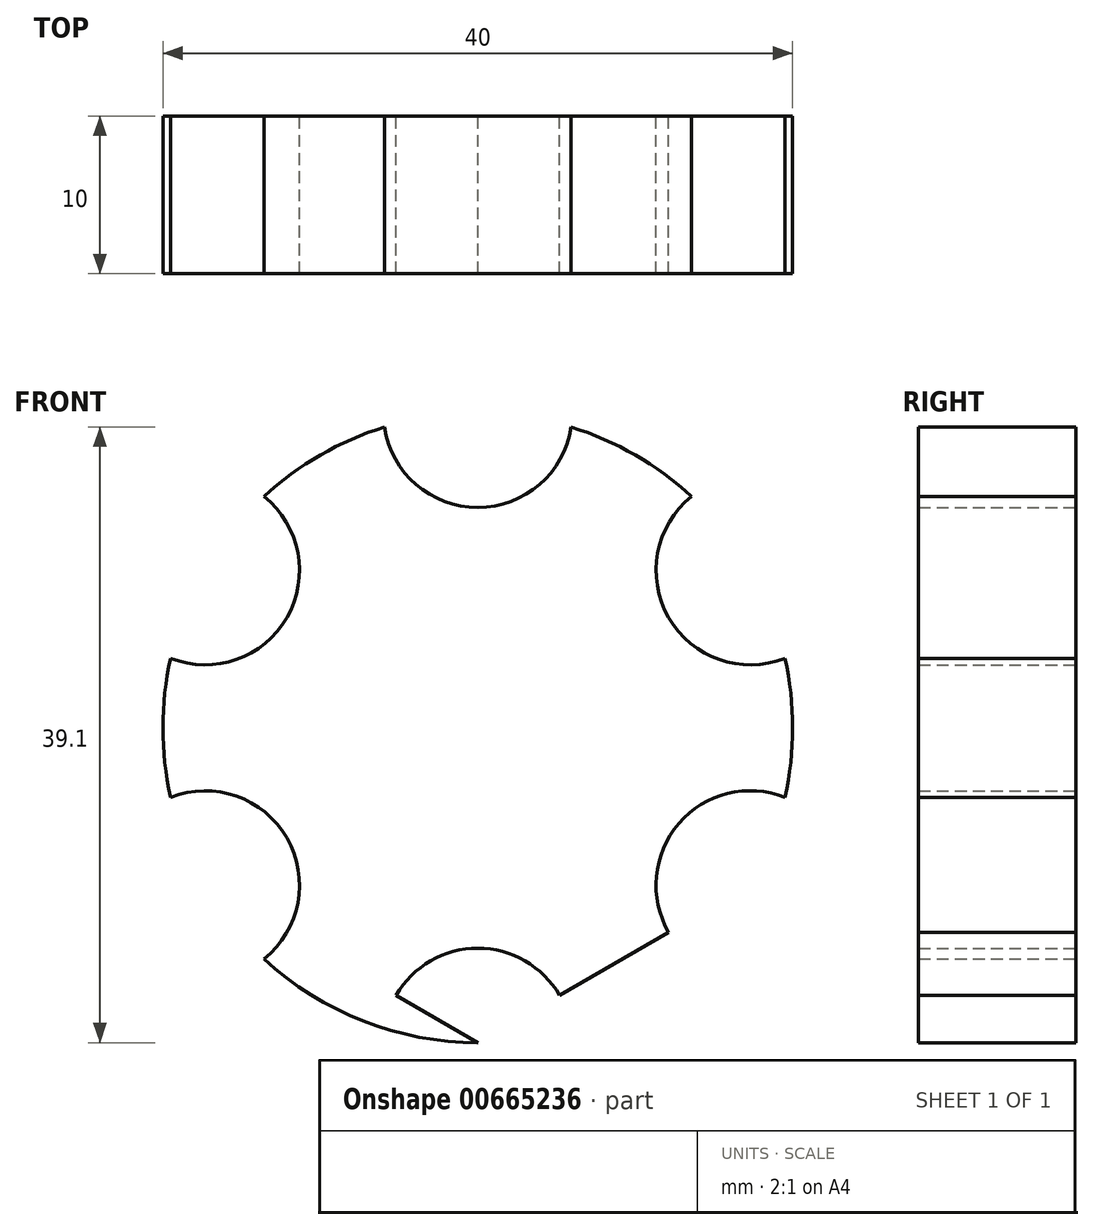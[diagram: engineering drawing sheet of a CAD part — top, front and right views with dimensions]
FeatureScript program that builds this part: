
annotation { "Feature Type Name" : "Feature", "Feature Type Description" : "" }
export const myFeature = defineFeature(function(context is Context, id is Id, definition is map)
    precondition{}
    {
        {
            var Q0;
            Q0=qCreatedBy(makeId("Front.planeOp"),FACE);
            cPlane(context, id + "F0", {"entities" : qUnion([Q0]), "cplaneType" : CPlaneType.OFFSET, "offset" : 20 * mm, "oppositeDirection" : true, "width" : 150 * mm, "height" : 150 * mm});
        }
        {
            var Q0;
            Q0=qCreatedBy(id+"F0.planeOp",FACE);
            var sketch = newSketch(context, id + "F1", { "sketchPlane" : qUnion([Q0])});
            skCircle(sketch, "E0", {"center": v(0, 0) * mm, "radius": 20 * mm});
            skCircle(sketch, "E1.cCircle", {"center": v(0, 0) * mm, "radius": 20 * mm, "construction": true});
            skLineSegment(sketch, "E1.0", {"start": v(0, 20) * mm, "end": v(17.32, 10) * mm});
            skLineSegment(sketch, "E1.1", {"start": v(17.32, 10) * mm, "end": v(17.32, -10) * mm});
            skLineSegment(sketch, "E1.2", {"start": v(17.32, -10) * mm, "end": v(0, -20) * mm});
            skLineSegment(sketch, "E1.3", {"start": v(0, -20) * mm, "end": v(-17.32, -10) * mm});
            skLineSegment(sketch, "E1.4", {"start": v(-17.32, -10) * mm, "end": v(-17.32, 10) * mm});
            skLineSegment(sketch, "E1.5", {"start": v(-17.32, 10) * mm, "end": v(0, 20) * mm});
            skCircle(sketch, "E2", {"center": v(0, 20) * mm, "radius": 6 * mm});
            skCircle(sketch, "E3", {"center": v(17.32, 10) * mm, "radius": 6 * mm});
            skCircle(sketch, "E4", {"center": v(0, -20) * mm, "radius": 6 * mm});
            skCircle(sketch, "E5", {"center": v(-17.32, 10) * mm, "radius": 6 * mm});
            skCircle(sketch, "E6", {"center": v(-17.32, -10) * mm, "radius": 6 * mm});
            skCircle(sketch, "E7", {"center": v(17.32, -10) * mm, "radius": 6 * mm});
            skSolve(sketch);
        }
        {
            var Q0;
            {var subQ0=sQuery(id+"F1.wireOp",EDGE,"E3");var subQ1=sQuery(id+"F1.wireOp",EDGE,"E0");var subQ2=makeQuery(id+"F1.imprint","INTERSECT",VERTEX,{"disambiguationData":[OD(1.0)],"derivedFrom":[subQ1,subQ0]});Q0=makeQuery(id+"F1.imprint","IMPRINT",FACE,{"disambiguationData":[TD([[makeQuery(id+"F1.imprint","IMPRINT",EDGE,{"disambiguationData":[TD([[subQ2,-1.0]])],"derivedFrom":subQ1}),1.0]])]});}
            var Q1;
            {var subQ0=sQuery(id+"F1.wireOp",EDGE,"E3");var subQ1=sQuery(id+"F1.wireOp",EDGE,"E0");var subQ2=makeQuery(id+"F1.imprint","INTERSECT",VERTEX,{"disambiguationData":[OD(0.0)],"derivedFrom":[subQ1,subQ0]});Q1=makeQuery(id+"F1.imprint","IMPRINT",FACE,{"disambiguationData":[TD([[makeQuery(id+"F1.imprint","IMPRINT",EDGE,{"disambiguationData":[TD([[subQ2,1.0]])],"derivedFrom":subQ1}),1.0]])]});}
            var Q2;
            {var subQ10=sQuery(id+"F1.wireOp",EDGE,"E2");var subQ11=sQuery(id+"F1.wireOp",EDGE,"E1.0");var subQ12=makeQuery(id+"F1.imprint","INTERSECT",VERTEX,{"derivedFrom":[subQ11,subQ10]});Q2=makeQuery(id+"F1.imprint","IMPRINT",FACE,{"disambiguationData":[TD([[makeQuery(id+"F1.imprint","IMPRINT",EDGE,{"disambiguationData":[TD([[subQ12,-1.0]])],"derivedFrom":subQ11}),-1.0]])]});}
            var Q3;
            {var subQ0=sQuery(id+"F1.wireOp",EDGE,"E4");var subQ1=sQuery(id+"F1.wireOp",EDGE,"E0");var subQ2=makeQuery(id+"F1.imprint","INTERSECT",VERTEX,{"disambiguationData":[OD(1.0)],"derivedFrom":[subQ1,subQ0]});Q3=makeQuery(id+"F1.imprint","IMPRINT",FACE,{"disambiguationData":[TD([[makeQuery(id+"F1.imprint","IMPRINT",EDGE,{"disambiguationData":[TD([[subQ2,-1.0]])],"derivedFrom":subQ1}),1.0]])]});}
            var Q4;
            {var subQ0=sQuery(id+"F1.wireOp",EDGE,"E6");var subQ1=sQuery(id+"F1.wireOp",EDGE,"E0");var subQ2=makeQuery(id+"F1.imprint","INTERSECT",VERTEX,{"disambiguationData":[OD(1.0)],"derivedFrom":[subQ1,subQ0]});Q4=makeQuery(id+"F1.imprint","IMPRINT",FACE,{"disambiguationData":[TD([[makeQuery(id+"F1.imprint","IMPRINT",EDGE,{"disambiguationData":[TD([[subQ2,-1.0]])],"derivedFrom":subQ1}),1.0]])]});}
            var Q5;
            {var subQ0=sQuery(id+"F1.wireOp",EDGE,"E2");var subQ1=sQuery(id+"F1.wireOp",EDGE,"E0");var subQ2=makeQuery(id+"F1.imprint","INTERSECT",VERTEX,{"disambiguationData":[OD(1.0)],"derivedFrom":[subQ1,subQ0]});Q5=makeQuery(id+"F1.imprint","IMPRINT",FACE,{"disambiguationData":[TD([[makeQuery(id+"F1.imprint","IMPRINT",EDGE,{"disambiguationData":[TD([[subQ2,-1.0]])],"derivedFrom":subQ1}),1.0]])]});}
            var Q6;
            {var subQ0=sQuery(id+"F1.wireOp",EDGE,"E5");var subQ1=sQuery(id+"F1.wireOp",EDGE,"E0");var subQ2=makeQuery(id+"F1.imprint","INTERSECT",VERTEX,{"disambiguationData":[OD(1.0)],"derivedFrom":[subQ1,subQ0]});Q6=makeQuery(id+"F1.imprint","IMPRINT",FACE,{"disambiguationData":[TD([[makeQuery(id+"F1.imprint","IMPRINT",EDGE,{"disambiguationData":[TD([[subQ2,-1.0]])],"derivedFrom":subQ1}),1.0]])]});}
            extrude(context, id + "F2", {"entities" : qUnion([Q0, Q1, Q2, Q3, Q4, Q5, Q6]), "depth" : 10 * mm, "offsetDistance" : 25 * mm});
        }
    });
